# Revit family: Neri_Light Nova_SUN03L-Pooo
name_source: partatom
category: Apparecchi per illuminazione
revit_build: Autodesk Revit LT 2018 (Build: 20170223_1515(x64)
units: mm (PartAtom-declared; Revit-internal decimal feet)

## family parameters
Basato su piano di lavoro = No
Condiviso = No
Numero OmniClass = 23.35.47.11
Punto di calcolo locali = No
Quota connettore circolare = Usa diametro
Sempre verticale = Sì
Sorgente d'illuminazione = Sì
Taglio con vuoti quando caricato = No
Tipo di parte = Normale

## types (6) — shared parameters
Angolo inclinazione = 90.00°
CRI = >70
Class IES = Full CutOff
Connection = Suspended installation with threaded tube (G 3/4")
Control = COD 02= 1-10V + NCL
Data Sheet = https://www.nerinorthamerica.com
Design Country = Italy
Diameter = 1' - 2 3/4"
EPA = 0.753 ft²
Estimated Life = 100.000 h (L85 - Ta 25°C)
Fasteners = Stainless Steel
Filtro dei colori = 16777215
Frequency = 50-60 Hz
Height = 1' - 3 3/4"
Height of Installation = From 13.5' to 25.5'
IK = 08
IP = 66
Immagine tipo = <Nessuno>
Installation Instructions = https://www.nerinorthamerica.com
LOR = 100 %
Lampada = LED
Luminous Efficacy = 107 Lm/W
Manufacturer Country = Italy
Manufacturer Name = Neri SpA
MasterFormat 2016 Code = 26 56 00
MasterFormat 2016 Description = Exterior Lighting
Material Main = Die-Cast  Aluminum
Material Secondary = Aluminum, White Matt RAL 9010
Modello = SUN03L-P
NBS_UniClass2015 Code = Ss_70_80_25_70
NBS_UniClass2015 Description = Roadway Lighting Systems
OmniClass Code = 23-35 47 11
OmniClass Description = Lighting Fixtures
Operative Temperature = -22°F / +104°F
Overvoltage Protection = 4kV/4kV (differential / common mode)
Painting = Standard color: Neri Gray on th upper part, White matt RAL 9010 on the lower part - On demand features - Painting:colour of RAL range
Painting Steps = Information about paint steps used in this product in specific technical sheet
Product Certification = UL Standard 1598 (C, US)
Product Name = Light Nova - LED P
Produttore = Neri SpA
SDCM = 5 Steps
Screen = Extra-clear transparent flat glass
URL = https://www.nerinorthamerica.com
UniFormat II Code = D5020
UniFormat II Description = Lighting and Branch Wiring
Variazione temperatura colore lampada con luminosità attenuata = <Nessuno>
Voltage = 120-277 V
W = 56
Weight = 23.15 lb

## per-type parameters (varying)
| type | File diagramma fotometrico | Lighting Distribution/Class | Luminaire Classification System | Optics |
| SUN03L_NLG17 | SUN03L_NLG17.IES | Asymmetric - Roadways - mixed areas (Type IV) | BUG: B1 U0 G1 | NLG17 |
| SUN03L_NLG18 | SUN03L_NLG18.IES | Rotosymmetrical - Mixed areas (Type V) | BUG: B2 U0 G0 | NLG18 |
| SUN03L_NLG19 | SUN03L_NLG19.IES | Asymmetric -Roadways - Center road installation (Type I) | BUG: B2 U0 G2 | NLG19 |
| SUN03L_NLG20 | SUN03L_NLG20.IES | Asymmetric -Roadways - Side road installation (Type II) | BUG: B2 U0 G1 | NLG20 |
| SUN03L_NLG21 | SUN03L_NLG21.IES | Asymmetric -Roadways with sidewalk (Type III) | BUG: B1 U0 G1 | NLG21 |
| SUN03L_NLG22 | SUN03L_NLG22.IES | Asymmetric -Roadways with sidewalk (Type III) | BUG: B1 U0 G1 | NLG22 |
